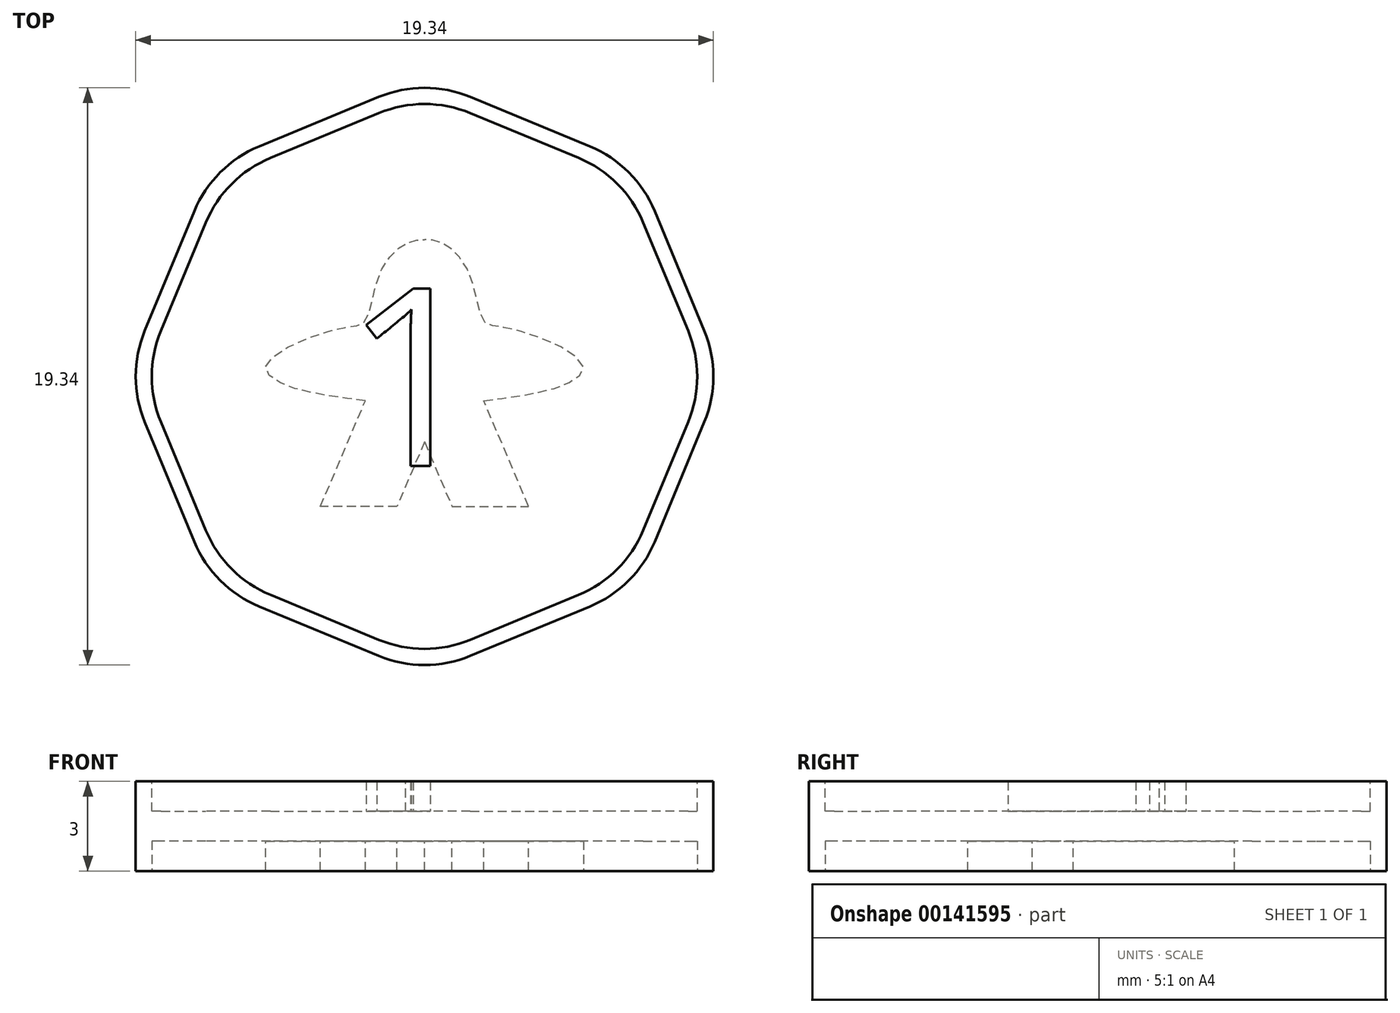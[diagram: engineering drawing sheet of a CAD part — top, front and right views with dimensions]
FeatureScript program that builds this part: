
annotation { "Feature Type Name" : "Feature", "Feature Type Description" : "" }
export const myFeature = defineFeature(function(context is Context, id is Id, definition is map)
    precondition{}
    {
        {
            assignVariable(context, id + "F0", {"name" : "Thickness", "anyValue" : 3});
        }
        {
            assignVariable(context, id + "F1", {"name" : "ImpressionDepth", "anyValue" : 1});
        }
        {
            var Q0;
            Q0=qCreatedBy(makeId("Top.planeOp"),FACE);
            var sketch = newSketch(context, id + "F2", { "sketchPlane" : qUnion([Q0])});
            skCircle(sketch, "E0.cCircle", {"center": v(0, 0) * mm, "radius": 10 * mm, "construction": true});
            skLineSegment(sketch, "E0.0", {"start": v(9.37, -1.53) * mm, "end": v(7.7, -5.54) * mm});
            skLineSegment(sketch, "E0.1", {"start": v(5.54, -7.7) * mm, "end": v(1.53, -9.37) * mm});
            skLineSegment(sketch, "E0.2", {"start": v(-1.53, -9.37) * mm, "end": v(-5.54, -7.7) * mm});
            skLineSegment(sketch, "E0.3", {"start": v(-7.7, -5.54) * mm, "end": v(-9.37, -1.53) * mm});
            skLineSegment(sketch, "E0.4", {"start": v(-9.37, 1.53) * mm, "end": v(-7.7, 5.54) * mm});
            skLineSegment(sketch, "E0.5", {"start": v(-5.54, 7.7) * mm, "end": v(-1.53, 9.37) * mm});
            skLineSegment(sketch, "E0.6", {"start": v(1.53, 9.37) * mm, "end": v(5.54, 7.7) * mm});
            skLineSegment(sketch, "E0.7", {"start": v(7.7, 5.54) * mm, "end": v(9.37, 1.53) * mm});
            skPoint(sketch, "E1.visualSharp", {"position": v(-7.07, 7.07) * mm});
            skArc(sketch, "E1.filletArc", {"start": v(-5.54, 7.7) * mm, "mid": v(-6.84, 6.84) * mm, "end": v(-7.7, 5.54) * mm});
            skPoint(sketch, "E2.visualSharp", {"position": v(0, 10) * mm});
            skArc(sketch, "E2.filletArc", {"start": v(1.53, 9.37) * mm, "mid": v(0, 9.67) * mm, "end": v(-1.53, 9.37) * mm});
            skPoint(sketch, "E3.visualSharp", {"position": v(7.07, 7.07) * mm});
            skArc(sketch, "E3.filletArc", {"start": v(7.7, 5.54) * mm, "mid": v(6.84, 6.84) * mm, "end": v(5.54, 7.7) * mm});
            skPoint(sketch, "E4.visualSharp", {"position": v(10, 0) * mm});
            skArc(sketch, "E4.filletArc", {"start": v(9.37, -1.53) * mm, "mid": v(9.67, 0) * mm, "end": v(9.37, 1.53) * mm});
            skPoint(sketch, "E5.visualSharp", {"position": v(-10, 0) * mm});
            skArc(sketch, "E5.filletArc", {"start": v(-9.37, 1.53) * mm, "mid": v(-9.67, 0) * mm, "end": v(-9.37, -1.53) * mm});
            skPoint(sketch, "E6.visualSharp", {"position": v(-7.07, -7.07) * mm});
            skArc(sketch, "E6.filletArc", {"start": v(-7.7, -5.54) * mm, "mid": v(-6.84, -6.84) * mm, "end": v(-5.54, -7.7) * mm});
            skPoint(sketch, "E7.visualSharp", {"position": v(0, -10) * mm});
            skArc(sketch, "E7.filletArc", {"start": v(-1.53, -9.37) * mm, "mid": v(0, -9.67) * mm, "end": v(1.53, -9.37) * mm});
            skPoint(sketch, "E8.visualSharp", {"position": v(7.07, -7.07) * mm});
            skArc(sketch, "E8.filletArc", {"start": v(5.54, -7.7) * mm, "mid": v(6.84, -6.84) * mm, "end": v(7.7, -5.54) * mm});
            skSolve(sketch);
        }
        {
            var Q0;
            Q0 = qSketchRegion(id + "F2", true);
            extrude(context, id + "F3", {"entities" : qUnion([Q0]), "oppositeDirection" : true, "depth" : (getVariable(context, 'Thickness')) * mm});
        }
        {
            var Q0;
            Q0=makeQuery(id+"F3.opExtrude","CAP_FACE",FACE,{"disambiguationData":[OSD([sQuery(id+"F2.wireOp",EDGE,"E0.0"),sQuery(id+"F2.wireOp",EDGE,"E0.1"),sQuery(id+"F2.wireOp",EDGE,"E0.2"),sQuery(id+"F2.wireOp",EDGE,"E0.3"),sQuery(id+"F2.wireOp",EDGE,"E0.4"),sQuery(id+"F2.wireOp",EDGE,"E0.5"),sQuery(id+"F2.wireOp",EDGE,"E0.6"),sQuery(id+"F2.wireOp",EDGE,"E0.7")])],"isStart":true});
            var sketch = newSketch(context, id + "F4", { "sketchPlane" : qUnion([Q0])});
            skLineSegment(sketch, "E9.0", {"start": v(-7.32, -5.16) * mm, "end": v(-8.82, -1.53) * mm});
            skLineSegment(sketch, "E9.1", {"start": v(-1.53, -8.82) * mm, "end": v(-5.16, -7.32) * mm});
            skLineSegment(sketch, "E9.2", {"start": v(-8.82, 1.53) * mm, "end": v(-7.32, 5.16) * mm});
            skLineSegment(sketch, "E9.3", {"start": v(5.16, -7.32) * mm, "end": v(1.53, -8.82) * mm});
            skLineSegment(sketch, "E9.4", {"start": v(-5.16, 7.32) * mm, "end": v(-1.53, 8.82) * mm});
            skLineSegment(sketch, "E9.5", {"start": v(1.53, 8.82) * mm, "end": v(5.16, 7.32) * mm});
            skLineSegment(sketch, "E9.6", {"start": v(7.32, 5.16) * mm, "end": v(8.82, 1.53) * mm});
            skLineSegment(sketch, "E9.7", {"start": v(8.82, -1.53) * mm, "end": v(7.32, -5.16) * mm});
            skPoint(sketch, "E10.visualSharp", {"position": v(-6.69, 6.69) * mm});
            skArc(sketch, "E10.filletArc", {"start": v(-5.16, 7.32) * mm, "mid": v(-6.46, 6.46) * mm, "end": v(-7.32, 5.16) * mm});
            skPoint(sketch, "E11.visualSharp", {"position": v(0, 9.46) * mm});
            skArc(sketch, "E11.filletArc", {"start": v(1.53, 8.82) * mm, "mid": v(0, 9.13) * mm, "end": v(-1.53, 8.82) * mm});
            skPoint(sketch, "E12.visualSharp", {"position": v(6.69, 6.69) * mm});
            skArc(sketch, "E12.filletArc", {"start": v(7.32, 5.16) * mm, "mid": v(6.46, 6.46) * mm, "end": v(5.16, 7.32) * mm});
            skPoint(sketch, "E13.visualSharp", {"position": v(9.46, 0) * mm});
            skArc(sketch, "E13.filletArc", {"start": v(8.82, -1.53) * mm, "mid": v(9.13, 0) * mm, "end": v(8.82, 1.53) * mm});
            skPoint(sketch, "E14.visualSharp", {"position": v(6.69, -6.69) * mm});
            skArc(sketch, "E14.filletArc", {"start": v(5.16, -7.32) * mm, "mid": v(6.46, -6.46) * mm, "end": v(7.32, -5.16) * mm});
            skPoint(sketch, "E15.visualSharp", {"position": v(0, -9.46) * mm});
            skArc(sketch, "E15.filletArc", {"start": v(-1.53, -8.82) * mm, "mid": v(0, -9.13) * mm, "end": v(1.53, -8.82) * mm});
            skPoint(sketch, "E16.visualSharp", {"position": v(-6.69, -6.69) * mm});
            skArc(sketch, "E16.filletArc", {"start": v(-7.32, -5.16) * mm, "mid": v(-6.46, -6.46) * mm, "end": v(-5.16, -7.32) * mm});
            skPoint(sketch, "E17.visualSharp", {"position": v(-9.46, 0) * mm});
            skArc(sketch, "E17.filletArc", {"start": v(-8.82, 1.53) * mm, "mid": v(-9.13, 0) * mm, "end": v(-8.82, -1.53) * mm});
            skSolve(sketch);
        }
        {
            var Q0;
            Q0 = qSketchRegion(id + "F4", true);
            extrude(context, id + "F5", {"entities" : qUnion([Q0]), "operationType" : NewBodyOperationType.REMOVE, "oppositeDirection" : true, "depth" : (getVariable(context, 'ImpressionDepth')) * mm});
        }
        {
            var Q0;
            Q0=makeQuery(id+"F3.opExtrude","CAP_FACE",FACE,{"disambiguationData":[OSD([sQuery(id+"F2.wireOp",EDGE,"E0.0"),sQuery(id+"F2.wireOp",EDGE,"E0.1"),sQuery(id+"F2.wireOp",EDGE,"E0.2"),sQuery(id+"F2.wireOp",EDGE,"E0.3"),sQuery(id+"F2.wireOp",EDGE,"E0.4"),sQuery(id+"F2.wireOp",EDGE,"E0.5"),sQuery(id+"F2.wireOp",EDGE,"E0.6"),sQuery(id+"F2.wireOp",EDGE,"E0.7")])],"isStart":false});
            var sketch = newSketch(context, id + "F6", { "sketchPlane" : qUnion([Q0])});
            skLineSegment(sketch, "E18.0", {"start": v(-8.82, -1.53) * mm, "end": v(-7.32, -5.16) * mm});
            skLineSegment(sketch, "E18.1", {"start": v(-7.32, 5.16) * mm, "end": v(-8.82, 1.53) * mm});
            skLineSegment(sketch, "E18.2", {"start": v(-5.16, -7.32) * mm, "end": v(-1.53, -8.82) * mm});
            skLineSegment(sketch, "E18.3", {"start": v(-1.53, 8.82) * mm, "end": v(-5.16, 7.32) * mm});
            skLineSegment(sketch, "E18.4", {"start": v(1.53, -8.82) * mm, "end": v(5.16, -7.32) * mm});
            skLineSegment(sketch, "E18.5", {"start": v(7.32, -5.16) * mm, "end": v(8.82, -1.53) * mm});
            skLineSegment(sketch, "E18.6", {"start": v(8.82, 1.53) * mm, "end": v(7.32, 5.16) * mm});
            skLineSegment(sketch, "E18.7", {"start": v(5.16, 7.32) * mm, "end": v(1.53, 8.82) * mm});
            skPoint(sketch, "E19.visualSharp", {"position": v(-6.69, 6.69) * mm});
            skArc(sketch, "E19.filletArc", {"start": v(-5.16, 7.32) * mm, "mid": v(-6.46, 6.46) * mm, "end": v(-7.32, 5.16) * mm});
            skPoint(sketch, "E20.visualSharp", {"position": v(0, 9.46) * mm});
            skArc(sketch, "E20.filletArc", {"start": v(1.53, 8.82) * mm, "mid": v(0, 9.13) * mm, "end": v(-1.53, 8.82) * mm});
            skPoint(sketch, "E21.visualSharp", {"position": v(6.69, 6.69) * mm});
            skArc(sketch, "E21.filletArc", {"start": v(7.32, 5.16) * mm, "mid": v(6.46, 6.46) * mm, "end": v(5.16, 7.32) * mm});
            skPoint(sketch, "E22.visualSharp", {"position": v(9.46, 0) * mm});
            skArc(sketch, "E22.filletArc", {"start": v(8.82, -1.53) * mm, "mid": v(9.13, 0) * mm, "end": v(8.82, 1.53) * mm});
            skPoint(sketch, "E23.visualSharp", {"position": v(6.69, -6.69) * mm});
            skArc(sketch, "E23.filletArc", {"start": v(5.16, -7.32) * mm, "mid": v(6.46, -6.46) * mm, "end": v(7.32, -5.16) * mm});
            skPoint(sketch, "E24.visualSharp", {"position": v(0, -9.46) * mm});
            skArc(sketch, "E24.filletArc", {"start": v(-1.53, -8.82) * mm, "mid": v(0, -9.13) * mm, "end": v(1.53, -8.82) * mm});
            skPoint(sketch, "E25.visualSharp", {"position": v(-6.69, -6.69) * mm});
            skArc(sketch, "E25.filletArc", {"start": v(-7.32, -5.16) * mm, "mid": v(-6.46, -6.46) * mm, "end": v(-5.16, -7.32) * mm});
            skPoint(sketch, "E26.visualSharp", {"position": v(-9.46, 0) * mm});
            skArc(sketch, "E26.filletArc", {"start": v(-8.82, 1.53) * mm, "mid": v(-9.13, 0) * mm, "end": v(-8.82, -1.53) * mm});
            skSolve(sketch);
        }
        {
            var Q0;
            Q0 = qSketchRegion(id + "F6", true);
            extrude(context, id + "F7", {"entities" : qUnion([Q0]), "operationType" : NewBodyOperationType.REMOVE, "oppositeDirection" : true, "depth" : (getVariable(context, 'ImpressionDepth')) * mm});
        }
        {
            var Q0;
            Q0=makeQuery(id+"F5.boolean.opBoolean","COPY",FACE,{"derivedFrom":makeQuery(id+"F5.opExtrude","CAP_FACE",FACE,{"disambiguationData":[OSD([sQuery(id+"F4.wireOp",EDGE,"E9.0"),sQuery(id+"F4.wireOp",EDGE,"E9.1"),sQuery(id+"F4.wireOp",EDGE,"E9.2"),sQuery(id+"F4.wireOp",EDGE,"E9.3"),sQuery(id+"F4.wireOp",EDGE,"E9.4"),sQuery(id+"F4.wireOp",EDGE,"E9.5"),sQuery(id+"F4.wireOp",EDGE,"E9.6"),sQuery(id+"F4.wireOp",EDGE,"E9.7"),sQuery(id+"F4.wireOp",EDGE,"E10.filletArc"),sQuery(id+"F4.wireOp",EDGE,"E11.filletArc"),sQuery(id+"F4.wireOp",EDGE,"E12.filletArc"),sQuery(id+"F4.wireOp",EDGE,"E13.filletArc"),sQuery(id+"F4.wireOp",EDGE,"E14.filletArc"),sQuery(id+"F4.wireOp",EDGE,"E15.filletArc"),sQuery(id+"F4.wireOp",EDGE,"E16.filletArc"),sQuery(id+"F4.wireOp",EDGE,"E17.filletArc")])],"isStart":false})});
            var sketch = newSketch(context, id + "F8", { "sketchPlane" : qUnion([Q0])});
            skText(sketch, "E27", { "text": "1", "fontName": "OpenSans-Regular.ttf"});
            skPoint(sketch, "E28", {"position": v(-1, 0) * mm});
            const initialGuessF8  = {"E27": [-0.00272, -0.003, 1, 0, 0.006]};
            skSetInitialGuess(sketch, initialGuessF8);
            skSolve(sketch);
        }
        {
            var Q0;
            Q0 = qSketchRegion(id + "F8", true);
            extrude(context, id + "F9", {"entities" : qUnion([Q0]), "operationType" : NewBodyOperationType.ADD, "depth" : (getVariable(context, 'ImpressionDepth')) * mm});
        }
        {
            var Q0;
            Q0=makeQuery(id+"F7.boolean.opBoolean","COPY",FACE,{"derivedFrom":makeQuery(id+"F7.opExtrude","CAP_FACE",FACE,{"disambiguationData":[OSD([sQuery(id+"F6.wireOp",EDGE,"E18.0"),sQuery(id+"F6.wireOp",EDGE,"E18.1"),sQuery(id+"F6.wireOp",EDGE,"E18.2"),sQuery(id+"F6.wireOp",EDGE,"E18.3"),sQuery(id+"F6.wireOp",EDGE,"E18.4"),sQuery(id+"F6.wireOp",EDGE,"E18.5"),sQuery(id+"F6.wireOp",EDGE,"E18.6"),sQuery(id+"F6.wireOp",EDGE,"E18.7"),sQuery(id+"F6.wireOp",EDGE,"E19.filletArc"),sQuery(id+"F6.wireOp",EDGE,"E20.filletArc"),sQuery(id+"F6.wireOp",EDGE,"E21.filletArc"),sQuery(id+"F6.wireOp",EDGE,"E22.filletArc"),sQuery(id+"F6.wireOp",EDGE,"E23.filletArc"),sQuery(id+"F6.wireOp",EDGE,"E24.filletArc"),sQuery(id+"F6.wireOp",EDGE,"E25.filletArc"),sQuery(id+"F6.wireOp",EDGE,"E26.filletArc")])],"isStart":false})});
            var sketch = newSketch(context, id + "F10", { "sketchPlane" : qUnion([Q0])});
            skLineSegment(sketch, "E29", {"start": v(0, -9.13) * mm, "end": v(0, 9.13) * mm, "construction": true});
            skLineSegment(sketch, "E30", {"start": v(0, 2.19) * mm, "end": v(-0.92, 4.36) * mm});
            skLineSegment(sketch, "E31", {"start": v(-0.92, 4.36) * mm, "end": v(-3.49, 4.36) * mm});
            skLineSegment(sketch, "E32", {"start": v(-3.49, 4.36) * mm, "end": v(-1.99, 0.82) * mm});
            skLineSegment(sketch, "E33.MirrorCS", {"start": v(0, 2.19) * mm, "end": v(0.92, 4.36) * mm});
            skLineSegment(sketch, "E34.MirrorCS", {"start": v(3.49, 4.36) * mm, "end": v(1.99, 0.82) * mm});
            skLineSegment(sketch, "E35.MirrorCS", {"start": v(0.92, 4.36) * mm, "end": v(3.49, 4.36) * mm});
            skFitSpline(sketch, "E36", {"points": [v(-1.99, 0.82) * mm, v(-4.54, 0.33) * mm, v(-5.3, -0.38) * mm, v(-2.81, -1.62) * mm, v(-1.99, -1.86) * mm, v(-1.48, -3.48) * mm, v(-0.56, -4.48) * mm, v(0, -4.58) * mm], "startDerivative": vector(-13.78, -2.1) * mm, "endDerivative": vector(6.01, 0) * mm});
            skFitSpline(sketch, "E37.MirrorCS", {"points": [v(1.99, 0.82) * mm, v(4.54, 0.33) * mm, v(5.3, -0.38) * mm, v(2.81, -1.62) * mm, v(1.99, -1.86) * mm, v(1.48, -3.48) * mm, v(0.56, -4.48) * mm, v(0, -4.58) * mm], "startDerivative": vector(13.78, -2.1) * mm, "endDerivative": vector(-6.01, 0) * mm});
            skPoint(sketch, "E38", {"position": v(0, 0) * mm});
            skSolve(sketch);
        }
        {
            var Q0;
            Q0 = qSketchRegion(id + "F10", true);
            extrude(context, id + "F11", {"entities" : qUnion([Q0]), "operationType" : NewBodyOperationType.ADD, "depth" : (getVariable(context, 'ImpressionDepth')) * mm});
        }
    });
